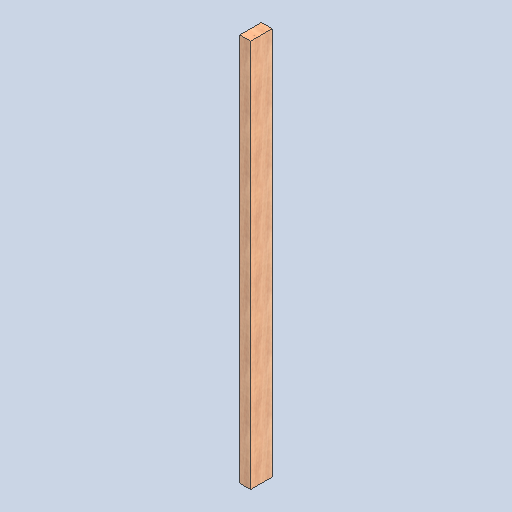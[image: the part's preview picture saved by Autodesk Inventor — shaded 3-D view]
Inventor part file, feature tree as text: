
AUTODESK INVENTOR PART (.ipt)
format: ipt  version: 2025 (Build 290162000, 162)  size: 117,248 bytes
history: native  units: in
note: dims shown in document units (in); Inventor stores cm internally (conversion verified against a paired STEP export)
features: other x3, sketch x1
ambient origin geometry x8: Origin, YZ Plane, XZ Plane, XY Plane, X Axis, Y Axis, Z Axis, Center Point
bodies: Solid1 (feature_tree)
feature tree (4):
  other  "2x4x72.ipt"
  other  "Solid1::2x4x72.ipt"
  other  "TaggingFeature1"
  sketch  "Sketch1"  dims[d0=0.3937in]
